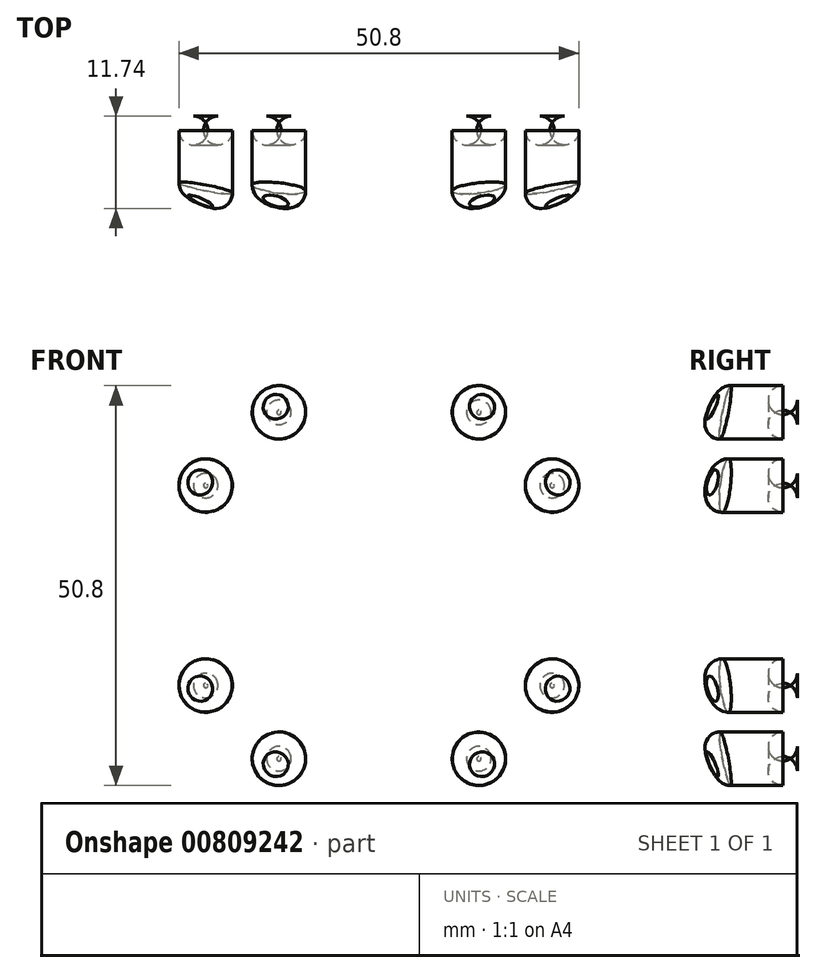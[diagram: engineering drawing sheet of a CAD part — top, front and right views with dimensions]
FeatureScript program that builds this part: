
annotation { "Feature Type Name" : "Feature", "Feature Type Description" : "" }
export const myFeature = defineFeature(function(context is Context, id is Id, definition is map)
    precondition{}
    {
        {
            var Q0;
            Q0=qCreatedBy(makeId("Front.planeOp"),FACE);
            var sketch = newSketch(context, id + "F0", { "sketchPlane" : qUnion([Q0])});
            skCircle(sketch, "E0", {"center": v(0, 0) * mm, "radius": 3.97 * mm});
            skCircle(sketch, "E1.cCircle", {"center": v(0, 0) * mm, "radius": 6.35 * mm, "construction": true});
            skLineSegment(sketch, "E1.0", {"start": v(-3.67, 6.35) * mm, "end": v(3.67, 6.35) * mm});
            skLineSegment(sketch, "E1.1", {"start": v(3.67, 6.35) * mm, "end": v(7.33, 0) * mm});
            skLineSegment(sketch, "E1.2", {"start": v(7.33, 0) * mm, "end": v(3.67, -6.35) * mm});
            skLineSegment(sketch, "E1.3", {"start": v(3.67, -6.35) * mm, "end": v(-3.67, -6.35) * mm});
            skLineSegment(sketch, "E1.4", {"start": v(-3.67, -6.35) * mm, "end": v(-7.33, 0) * mm});
            skLineSegment(sketch, "E1.5", {"start": v(-7.33, 0) * mm, "end": v(-3.67, 6.35) * mm});
            skPoint(sketch, "E1.0.midPoint", {"position": v(0, 6.35) * mm});
            skSolve(sketch);
        }
        {
            var Q0;
            Q0 = qSketchRegion(id + "F0", true);
            extrude(context, id + "F1", {"entities" : qUnion([Q0]), "depth" : 6.35 * mm, "offsetDistance" : 25.4 * mm});
        }
        {
            var Q0;
            Q0=qCreatedBy(makeId("Front.planeOp"),FACE);
            var sketch = newSketch(context, id + "F2", { "sketchPlane" : qUnion([Q0])});
            skLineSegment(sketch, "E2.0.0", {"start": v(-3.67, 6.35) * mm, "end": v(-7.33, 0) * mm});
            skLineSegment(sketch, "E2.0.1", {"start": v(-7.33, 0) * mm, "end": v(-3.67, -6.35) * mm});
            skLineSegment(sketch, "E2.0.2", {"start": v(-3.67, -6.35) * mm, "end": v(3.67, -6.35) * mm});
            skLineSegment(sketch, "E2.0.3", {"start": v(3.67, -6.35) * mm, "end": v(7.33, 0) * mm});
            skLineSegment(sketch, "E2.0.4", {"start": v(7.33, 0) * mm, "end": v(3.67, 6.35) * mm});
            skLineSegment(sketch, "E2.0.5", {"start": v(3.67, 6.35) * mm, "end": v(-3.67, 6.35) * mm});
            skCircle(sketch, "E3.cCircle", {"center": v(0, 0) * mm, "radius": 12.7 * mm, "construction": true});
            skLineSegment(sketch, "E3.1", {"start": v(3.4, 12.7) * mm, "end": v(9.3, 9.3) * mm});
            skLineSegment(sketch, "E3.2", {"start": v(9.3, 9.3) * mm, "end": v(12.7, 3.4) * mm});
            skLineSegment(sketch, "E3.3", {"start": v(12.7, 3.4) * mm, "end": v(12.7, -3.4) * mm});
            skLineSegment(sketch, "E3.4", {"start": v(12.7, -3.4) * mm, "end": v(9.3, -9.3) * mm});
            skLineSegment(sketch, "E3.5", {"start": v(9.3, -9.3) * mm, "end": v(3.4, -12.7) * mm});
            skLineSegment(sketch, "E3.6", {"start": v(3.4, -12.7) * mm, "end": v(-3.4, -12.7) * mm});
            skLineSegment(sketch, "E3.7", {"start": v(-3.4, -12.7) * mm, "end": v(-9.3, -9.3) * mm});
            skLineSegment(sketch, "E3.8", {"start": v(-9.3, -9.3) * mm, "end": v(-12.7, -3.4) * mm});
            skLineSegment(sketch, "E3.9", {"start": v(-12.7, -3.4) * mm, "end": v(-12.7, 3.4) * mm});
            skLineSegment(sketch, "E3.10", {"start": v(-12.7, 3.4) * mm, "end": v(-9.3, 9.3) * mm});
            skLineSegment(sketch, "E3.11", {"start": v(-9.3, 9.3) * mm, "end": v(-3.4, 12.7) * mm});
            skPoint(sketch, "E3.0.midPoint", {"position": v(0, 12.7) * mm});
            skLineSegment(sketch, "E4", {"start": v(-3.4, 12.7) * mm, "end": v(-3.4, 25.4) * mm});
            skLineSegment(sketch, "E5.bottom", {"start": v(3.4, 12.7) * mm, "end": v(-3.4, 12.7) * mm});
            skLineSegment(sketch, "E5.left", {"start": v(3.4, 12.7) * mm, "end": v(3.4, 25.4) * mm});
            skCircle(sketch, "E6", {"center": v(0, 25.4) * mm, "radius": 3.4 * mm});
            skCircle(sketch, "E7.1.0", {"center": v(-12.7, 22) * mm, "radius": 3.4 * mm});
            skLineSegment(sketch, "E7.1.1", {"start": v(-9.3, 9.3) * mm, "end": v(-15.65, 20.3) * mm});
            skLineSegment(sketch, "E7.1.2", {"start": v(-3.4, 12.7) * mm, "end": v(-9.75, 23.7) * mm});
            skCircle(sketch, "E7.2.0", {"center": v(-22, 12.7) * mm, "radius": 3.4 * mm});
            skLineSegment(sketch, "E7.2.1", {"start": v(-12.7, 3.4) * mm, "end": v(-23.7, 9.75) * mm});
            skLineSegment(sketch, "E7.2.2", {"start": v(-9.3, 9.3) * mm, "end": v(-20.3, 15.65) * mm});
            skCircle(sketch, "E7.3.0", {"center": v(-25.4, 0) * mm, "radius": 3.4 * mm});
            skLineSegment(sketch, "E7.3.1", {"start": v(-12.7, -3.4) * mm, "end": v(-25.4, -3.4) * mm});
            skLineSegment(sketch, "E7.3.2", {"start": v(-12.7, 3.4) * mm, "end": v(-25.4, 3.4) * mm});
            skCircle(sketch, "E7.4.0", {"center": v(-22, -12.7) * mm, "radius": 3.4 * mm});
            skLineSegment(sketch, "E7.4.1", {"start": v(-9.3, -9.3) * mm, "end": v(-20.3, -15.65) * mm});
            skLineSegment(sketch, "E7.4.2", {"start": v(-12.7, -3.4) * mm, "end": v(-23.7, -9.75) * mm});
            skCircle(sketch, "E7.5.0", {"center": v(-12.7, -22) * mm, "radius": 3.4 * mm});
            skLineSegment(sketch, "E7.5.1", {"start": v(-3.4, -12.7) * mm, "end": v(-9.75, -23.7) * mm});
            skLineSegment(sketch, "E7.5.2", {"start": v(-9.3, -9.3) * mm, "end": v(-15.65, -20.3) * mm});
            skCircle(sketch, "E7.6.0", {"center": v(0, -25.4) * mm, "radius": 3.4 * mm});
            skLineSegment(sketch, "E7.6.1", {"start": v(3.4, -12.7) * mm, "end": v(3.4, -25.4) * mm});
            skLineSegment(sketch, "E7.6.2", {"start": v(-3.4, -12.7) * mm, "end": v(-3.4, -25.4) * mm});
            skCircle(sketch, "E7.7.0", {"center": v(12.7, -22) * mm, "radius": 3.4 * mm});
            skLineSegment(sketch, "E7.7.1", {"start": v(9.3, -9.3) * mm, "end": v(15.65, -20.3) * mm});
            skLineSegment(sketch, "E7.7.2", {"start": v(3.4, -12.7) * mm, "end": v(9.75, -23.7) * mm});
            skCircle(sketch, "E7.8.0", {"center": v(22, -12.7) * mm, "radius": 3.4 * mm});
            skLineSegment(sketch, "E7.8.1", {"start": v(12.7, -3.4) * mm, "end": v(23.7, -9.75) * mm});
            skLineSegment(sketch, "E7.8.2", {"start": v(9.3, -9.3) * mm, "end": v(20.3, -15.65) * mm});
            skCircle(sketch, "E7.9.0", {"center": v(25.4, 0) * mm, "radius": 3.4 * mm});
            skLineSegment(sketch, "E7.9.1", {"start": v(12.7, 3.4) * mm, "end": v(25.4, 3.4) * mm});
            skLineSegment(sketch, "E7.9.2", {"start": v(12.7, -3.4) * mm, "end": v(25.4, -3.4) * mm});
            skCircle(sketch, "E7.10.0", {"center": v(22, 12.7) * mm, "radius": 3.4 * mm});
            skLineSegment(sketch, "E7.10.1", {"start": v(9.3, 9.3) * mm, "end": v(20.3, 15.65) * mm});
            skLineSegment(sketch, "E7.10.2", {"start": v(12.7, 3.4) * mm, "end": v(23.7, 9.75) * mm});
            skCircle(sketch, "E7.11.0", {"center": v(12.7, 22) * mm, "radius": 3.4 * mm});
            skLineSegment(sketch, "E7.11.1", {"start": v(3.4, 12.7) * mm, "end": v(9.75, 23.7) * mm});
            skLineSegment(sketch, "E7.11.2", {"start": v(9.3, 9.3) * mm, "end": v(15.65, 20.3) * mm});
            skSolve(sketch);
        }
        {
            var Q0;
            Q0 = qSketchRegion(id + "F2", true);
            extrude(context, id + "F3", {"entities" : qUnion([Q0]), "depth" : 6.35 * mm, "offsetDistance" : 25.4 * mm, "hasSecondDirection" : true, "secondDirectionOppositeDirection" : true, "secondDirectionDepth" : 6.35 * mm});
        }
        {
            var Q0;
            Q0=makeQuery(id+"F1.opExtrude","CAP_FACE",FACE,{"disambiguationData":[OSD([sQuery(id+"F0.wireOp",EDGE,"E0"),sQuery(id+"F0.wireOp",EDGE,"E1.0"),sQuery(id+"F0.wireOp",EDGE,"E1.1"),sQuery(id+"F0.wireOp",EDGE,"E1.2"),sQuery(id+"F0.wireOp",EDGE,"E1.3"),sQuery(id+"F0.wireOp",EDGE,"E1.4"),sQuery(id+"F0.wireOp",EDGE,"E1.5")])],"isStart":true});
            extrude(context, id + "F4", {"entities" : qUnion([Q0]), "operationType" : NewBodyOperationType.ADD, "depth" : 6.35 * mm, "offsetDistance" : 25.4 * mm});
        }
        {
            var Q0;
            {var subQ0=sQuery(id+"F2.wireOp",EDGE,"E7.1.0");var subQ1=makeQuery(id+"F2.imprint","INTERSECT",VERTEX,{"derivedFrom":[subQ0,sQuery(id+"F2.wireOp",EDGE,"E7.1.1")]});Q0=makeQuery(id+"F2.imprint","IMPRINT",FACE,{"disambiguationData":[TD([[makeQuery(id+"F2.imprint","IMPRINT",EDGE,{"disambiguationData":[TD([[subQ1,1.0]])],"derivedFrom":subQ0}),1.0]])]});}
            var Q1;
            {var subQ0=sQuery(id+"F2.wireOp",EDGE,"E6");var subQ1=makeQuery(id+"F2.imprint","INTERSECT",VERTEX,{"derivedFrom":[sQuery(id+"F2.wireOp",EDGE,"E5.left"),subQ0]});Q1=makeQuery(id+"F2.imprint","IMPRINT",FACE,{"disambiguationData":[TD([[makeQuery(id+"F2.imprint","IMPRINT",EDGE,{"disambiguationData":[TD([[subQ1,-1.0]])],"derivedFrom":subQ0}),1.0]])]});}
            var Q2;
            {var subQ0=sQuery(id+"F2.wireOp",EDGE,"E7.11.0");var subQ1=makeQuery(id+"F2.imprint","INTERSECT",VERTEX,{"derivedFrom":[subQ0,sQuery(id+"F2.wireOp",EDGE,"E7.11.1")]});Q2=makeQuery(id+"F2.imprint","IMPRINT",FACE,{"disambiguationData":[TD([[makeQuery(id+"F2.imprint","IMPRINT",EDGE,{"disambiguationData":[TD([[subQ1,1.0]])],"derivedFrom":subQ0}),1.0]])]});}
            var Q3;
            {var subQ0=sQuery(id+"F2.wireOp",EDGE,"E7.2.0");var subQ1=makeQuery(id+"F2.imprint","INTERSECT",VERTEX,{"derivedFrom":[subQ0,sQuery(id+"F2.wireOp",EDGE,"E7.2.1")]});Q3=makeQuery(id+"F2.imprint","IMPRINT",FACE,{"disambiguationData":[TD([[makeQuery(id+"F2.imprint","IMPRINT",EDGE,{"disambiguationData":[TD([[subQ1,1.0]])],"derivedFrom":subQ0}),1.0]])]});}
            var Q4;
            {var subQ0=sQuery(id+"F2.wireOp",EDGE,"E7.3.0");var subQ1=makeQuery(id+"F2.imprint","INTERSECT",VERTEX,{"derivedFrom":[subQ0,sQuery(id+"F2.wireOp",EDGE,"E7.3.1")]});Q4=makeQuery(id+"F2.imprint","IMPRINT",FACE,{"disambiguationData":[TD([[makeQuery(id+"F2.imprint","IMPRINT",EDGE,{"disambiguationData":[TD([[subQ1,1.0]])],"derivedFrom":subQ0}),1.0]])]});}
            var Q5;
            {var subQ0=sQuery(id+"F2.wireOp",EDGE,"E7.4.0");var subQ1=makeQuery(id+"F2.imprint","INTERSECT",VERTEX,{"derivedFrom":[subQ0,sQuery(id+"F2.wireOp",EDGE,"E7.4.1")]});Q5=makeQuery(id+"F2.imprint","IMPRINT",FACE,{"disambiguationData":[TD([[makeQuery(id+"F2.imprint","IMPRINT",EDGE,{"disambiguationData":[TD([[subQ1,1.0]])],"derivedFrom":subQ0}),1.0]])]});}
            var Q6;
            {var subQ0=sQuery(id+"F2.wireOp",EDGE,"E7.5.0");var subQ1=makeQuery(id+"F2.imprint","INTERSECT",VERTEX,{"derivedFrom":[subQ0,sQuery(id+"F2.wireOp",EDGE,"E7.5.1")]});Q6=makeQuery(id+"F2.imprint","IMPRINT",FACE,{"disambiguationData":[TD([[makeQuery(id+"F2.imprint","IMPRINT",EDGE,{"disambiguationData":[TD([[subQ1,1.0]])],"derivedFrom":subQ0}),1.0]])]});}
            var Q7;
            {var subQ0=sQuery(id+"F2.wireOp",EDGE,"E7.6.0");var subQ1=makeQuery(id+"F2.imprint","INTERSECT",VERTEX,{"derivedFrom":[subQ0,sQuery(id+"F2.wireOp",EDGE,"E7.6.1")]});Q7=makeQuery(id+"F2.imprint","IMPRINT",FACE,{"disambiguationData":[TD([[makeQuery(id+"F2.imprint","IMPRINT",EDGE,{"disambiguationData":[TD([[subQ1,1.0]])],"derivedFrom":subQ0}),1.0]])]});}
            var Q8;
            {var subQ0=sQuery(id+"F2.wireOp",EDGE,"E7.7.0");var subQ1=makeQuery(id+"F2.imprint","INTERSECT",VERTEX,{"derivedFrom":[subQ0,sQuery(id+"F2.wireOp",EDGE,"E7.7.1")]});Q8=makeQuery(id+"F2.imprint","IMPRINT",FACE,{"disambiguationData":[TD([[makeQuery(id+"F2.imprint","IMPRINT",EDGE,{"disambiguationData":[TD([[subQ1,1.0]])],"derivedFrom":subQ0}),1.0]])]});}
            var Q9;
            {var subQ0=sQuery(id+"F2.wireOp",EDGE,"E7.8.0");var subQ1=makeQuery(id+"F2.imprint","INTERSECT",VERTEX,{"derivedFrom":[subQ0,sQuery(id+"F2.wireOp",EDGE,"E7.8.1")]});Q9=makeQuery(id+"F2.imprint","IMPRINT",FACE,{"disambiguationData":[TD([[makeQuery(id+"F2.imprint","IMPRINT",EDGE,{"disambiguationData":[TD([[subQ1,1.0]])],"derivedFrom":subQ0}),1.0]])]});}
            var Q10;
            {var subQ0=sQuery(id+"F2.wireOp",EDGE,"E7.9.0");var subQ1=makeQuery(id+"F2.imprint","INTERSECT",VERTEX,{"derivedFrom":[subQ0,sQuery(id+"F2.wireOp",EDGE,"E7.9.1")]});Q10=makeQuery(id+"F2.imprint","IMPRINT",FACE,{"disambiguationData":[TD([[makeQuery(id+"F2.imprint","IMPRINT",EDGE,{"disambiguationData":[TD([[subQ1,1.0]])],"derivedFrom":subQ0}),1.0]])]});}
            var Q11;
            {var subQ0=sQuery(id+"F2.wireOp",EDGE,"E7.10.0");var subQ1=makeQuery(id+"F2.imprint","INTERSECT",VERTEX,{"derivedFrom":[subQ0,sQuery(id+"F2.wireOp",EDGE,"E7.10.1")]});Q11=makeQuery(id+"F2.imprint","IMPRINT",FACE,{"disambiguationData":[TD([[makeQuery(id+"F2.imprint","IMPRINT",EDGE,{"disambiguationData":[TD([[subQ1,1.0]])],"derivedFrom":subQ0}),1.0]])]});}
            extrude(context, id + "F5", {"entities" : qUnion([Q0, Q1, Q2, Q3, Q4, Q5, Q6, Q7, Q8, Q9, Q10, Q11]), "operationType" : NewBodyOperationType.ADD, "oppositeDirection" : true, "depth" : 12.7 * mm, "offsetDistance" : 25.4 * mm});
        }
        {
            var Q0;
            Q0=qCreatedBy(makeId("Right.planeOp"),FACE);
            var sketch = newSketch(context, id + "F6", { "sketchPlane" : qUnion([Q0])});
            skPoint(sketch, "E8.0", {"position": v(-6.35, 6.35) * mm});
            skPoint(sketch, "E9.0", {"position": v(-6.35, 9.3) * mm});
            skLineSegment(sketch, "E10", {"start": v(-6.35, 28.8) * mm, "end": v(12.7, 28.8) * mm});
            skPoint(sketch, "E11.0", {"position": v(6.35, 20.3) * mm});
            skLineSegment(sketch, "E12", {"start": v(6.35, 20.3) * mm, "end": v(6.35, 28.8) * mm, "construction": true});
            skLineSegment(sketch, "E13", {"start": v(3.17, 28.8) * mm, "end": v(-6.35, 9.3) * mm});
            skLineSegment(sketch, "E14", {"start": v(3.17, 28.8) * mm, "end": v(3.17, 31.54) * mm});
            skLineSegment(sketch, "E15", {"start": v(3.17, 31.54) * mm, "end": v(-9.41, 31.54) * mm});
            skLineSegment(sketch, "E16", {"start": v(-9.41, 31.54) * mm, "end": v(-8.74, 8.57) * mm});
            skLineSegment(sketch, "E17", {"start": v(-8.74, 8.57) * mm, "end": v(-6.35, 9.3) * mm});
            skSolve(sketch);
        }
        {
            var Q0;
            Q0 = qSketchRegion(id + "F6", true);
            var Q1;
            Q1=makeQuery(id+"F1.opExtrude","SWEPT_FACE",FACE,{"disambiguationData":[OSD([sQuery(id+"F0.wireOp",EDGE,"E0")])]});
            revolve(context, id + "F7", {"operationType" : NewBodyOperationType.REMOVE, "surfaceOperationType" : NewSurfaceOperationType.NEW, "entities" : qUnion([Q0]), "axis" : qUnion([Q1]), "revolveType" : RevolveType.FULL, "oppositeDirection" : true});
        }
        {
            var Q0;
            Q0=makeQuery(id+"F3.opExtrude","CAP_EDGE",EDGE,{"disambiguationData":[OSD([sQuery(id+"F2.wireOp",EDGE,"E4")])],"isStart":true});
            var Q1;
            Q1=makeQuery(id+"F3.opExtrude","CAP_EDGE",EDGE,{"disambiguationData":[OSD([sQuery(id+"F2.wireOp",EDGE,"E7.1.2")])],"isStart":true});
            var Q2;
            Q2=makeQuery(id+"F3.opExtrude","CAP_EDGE",EDGE,{"disambiguationData":[OSD([sQuery(id+"F2.wireOp",EDGE,"E7.2.2")])],"isStart":true});
            var Q3;
            Q3=makeQuery(id+"F3.opExtrude","CAP_EDGE",EDGE,{"disambiguationData":[OSD([sQuery(id+"F2.wireOp",EDGE,"E7.1.1")])],"isStart":true});
            var Q4;
            Q4=makeQuery(id+"F3.opExtrude","CAP_EDGE",EDGE,{"disambiguationData":[OSD([sQuery(id+"F2.wireOp",EDGE,"E7.2.1")])],"isStart":true});
            var Q5;
            Q5=makeQuery(id+"F3.opExtrude","CAP_EDGE",EDGE,{"disambiguationData":[OSD([sQuery(id+"F2.wireOp",EDGE,"E7.3.2")])],"isStart":true});
            var Q6;
            Q6=makeQuery(id+"F3.opExtrude","CAP_EDGE",EDGE,{"disambiguationData":[OSD([sQuery(id+"F2.wireOp",EDGE,"E7.3.1")])],"isStart":true});
            var Q7;
            Q7=makeQuery(id+"F3.opExtrude","CAP_EDGE",EDGE,{"disambiguationData":[OSD([sQuery(id+"F2.wireOp",EDGE,"E7.4.2")])],"isStart":true});
            var Q8;
            Q8=makeQuery(id+"F3.opExtrude","CAP_EDGE",EDGE,{"disambiguationData":[OSD([sQuery(id+"F2.wireOp",EDGE,"E7.4.1")])],"isStart":true});
            var Q9;
            Q9=makeQuery(id+"F3.opExtrude","CAP_EDGE",EDGE,{"disambiguationData":[OSD([sQuery(id+"F2.wireOp",EDGE,"E7.5.2")])],"isStart":true});
            var Q10;
            Q10=makeQuery(id+"F3.opExtrude","CAP_EDGE",EDGE,{"disambiguationData":[OSD([sQuery(id+"F2.wireOp",EDGE,"E7.6.2")])],"isStart":true});
            var Q11;
            Q11=makeQuery(id+"F3.opExtrude","CAP_EDGE",EDGE,{"disambiguationData":[OSD([sQuery(id+"F2.wireOp",EDGE,"E7.5.1")])],"isStart":true});
            var Q12;
            Q12=makeQuery(id+"F3.opExtrude","CAP_EDGE",EDGE,{"disambiguationData":[OSD([sQuery(id+"F2.wireOp",EDGE,"E7.6.1")])],"isStart":true});
            var Q13;
            Q13=makeQuery(id+"F3.opExtrude","CAP_EDGE",EDGE,{"disambiguationData":[OSD([sQuery(id+"F2.wireOp",EDGE,"E7.7.2")])],"isStart":true});
            var Q14;
            Q14=makeQuery(id+"F3.opExtrude","CAP_EDGE",EDGE,{"disambiguationData":[OSD([sQuery(id+"F2.wireOp",EDGE,"E7.8.2")])],"isStart":true});
            var Q15;
            Q15=makeQuery(id+"F3.opExtrude","CAP_EDGE",EDGE,{"disambiguationData":[OSD([sQuery(id+"F2.wireOp",EDGE,"E7.7.1")])],"isStart":true});
            var Q16;
            Q16=makeQuery(id+"F3.opExtrude","CAP_EDGE",EDGE,{"disambiguationData":[OSD([sQuery(id+"F2.wireOp",EDGE,"E7.9.2")])],"isStart":true});
            var Q17;
            Q17=makeQuery(id+"F3.opExtrude","CAP_EDGE",EDGE,{"disambiguationData":[OSD([sQuery(id+"F2.wireOp",EDGE,"E7.8.1")])],"isStart":true});
            var Q18;
            Q18=makeQuery(id+"F3.opExtrude","CAP_EDGE",EDGE,{"disambiguationData":[OSD([sQuery(id+"F2.wireOp",EDGE,"E7.10.2")])],"isStart":true});
            var Q19;
            Q19=makeQuery(id+"F3.opExtrude","CAP_EDGE",EDGE,{"disambiguationData":[OSD([sQuery(id+"F2.wireOp",EDGE,"E7.9.1")])],"isStart":true});
            var Q20;
            Q20=makeQuery(id+"F3.opExtrude","CAP_EDGE",EDGE,{"disambiguationData":[OSD([sQuery(id+"F2.wireOp",EDGE,"E7.10.1")])],"isStart":true});
            var Q21;
            Q21=makeQuery(id+"F3.opExtrude","CAP_EDGE",EDGE,{"disambiguationData":[OSD([sQuery(id+"F2.wireOp",EDGE,"E7.11.2")])],"isStart":true});
            var Q22;
            Q22=makeQuery(id+"F3.opExtrude","CAP_EDGE",EDGE,{"disambiguationData":[OSD([sQuery(id+"F2.wireOp",EDGE,"E7.11.1")])],"isStart":true});
            var Q23;
            Q23=makeQuery(id+"F3.opExtrude","CAP_EDGE",EDGE,{"disambiguationData":[OSD([sQuery(id+"F2.wireOp",EDGE,"E5.left")])],"isStart":true});
            var Q24;
            Q24=makeQuery(id+"F5.opExtrude","CAP_EDGE",EDGE,{"disambiguationData":[OSD([sQuery(id+"F2.wireOp",EDGE,"E7.11.0")])],"isStart":false});
            var Q25;
            Q25=makeQuery(id+"F5.opExtrude","CAP_FACE",FACE,{"disambiguationData":[OSD([sQuery(id+"F2.wireOp",EDGE,"E7.10.0")])],"isStart":false});
            var Q26;
            Q26=makeQuery(id+"F5.opExtrude","CAP_FACE",FACE,{"disambiguationData":[OSD([sQuery(id+"F2.wireOp",EDGE,"E7.9.0")])],"isStart":false});
            var Q27;
            Q27=makeQuery(id+"F5.opExtrude","CAP_FACE",FACE,{"disambiguationData":[OSD([sQuery(id+"F2.wireOp",EDGE,"E7.8.0")])],"isStart":false});
            var Q28;
            Q28=makeQuery(id+"F5.opExtrude","CAP_FACE",FACE,{"disambiguationData":[OSD([sQuery(id+"F2.wireOp",EDGE,"E7.7.0")])],"isStart":false});
            var Q29;
            Q29=makeQuery(id+"F5.opExtrude","CAP_FACE",FACE,{"disambiguationData":[OSD([sQuery(id+"F2.wireOp",EDGE,"E7.6.0")])],"isStart":false});
            var Q30;
            Q30=makeQuery(id+"F5.opExtrude","CAP_FACE",FACE,{"disambiguationData":[OSD([sQuery(id+"F2.wireOp",EDGE,"E7.5.0")])],"isStart":false});
            var Q31;
            Q31=makeQuery(id+"F5.opExtrude","CAP_EDGE",EDGE,{"disambiguationData":[OSD([sQuery(id+"F2.wireOp",EDGE,"E7.4.0")])],"isStart":false});
            var Q32;
            Q32=makeQuery(id+"F5.opExtrude","CAP_FACE",FACE,{"disambiguationData":[OSD([sQuery(id+"F2.wireOp",EDGE,"E7.3.0")])],"isStart":false});
            var Q33;
            Q33=makeQuery(id+"F5.opExtrude","CAP_FACE",FACE,{"disambiguationData":[OSD([sQuery(id+"F2.wireOp",EDGE,"E7.2.0")])],"isStart":false});
            var Q34;
            Q34=makeQuery(id+"F5.opExtrude","CAP_FACE",FACE,{"disambiguationData":[OSD([sQuery(id+"F2.wireOp",EDGE,"E7.1.0")])],"isStart":false});
            var Q35;
            Q35=makeQuery(id+"F5.opExtrude","CAP_FACE",FACE,{"disambiguationData":[OSD([sQuery(id+"F2.wireOp",EDGE,"E6")])],"isStart":false});
            var Q36;
            Q36=makeQuery(id+"F7.boolean.opBoolean","COPY",FACE,{"derivedFrom":makeQuery(id+"F7.opRevolve","SWEPT_FACE",FACE,{"disambiguationData":[OSD([sQuery(id+"F6.wireOp",EDGE,"E13")])]})});
            fillet(context, id + "F8", {"entities" : qUnion([Q0, Q1, Q2, Q3, Q4, Q5, Q6, Q7, Q8, Q9, Q10, Q11, Q12, Q13, Q14, Q15, Q16, Q17, Q18, Q19, Q20, Q21, Q22, Q23, Q24, Q25, Q26, Q27, Q28, Q29, Q30, Q31, Q32, Q33, Q34, Q35, Q36]), "radius" : 1.84 * mm, "tangentPropagation" : true, "allowEdgeOverflow" : false});
        }
        {
            var Q0;
            Q0=makeQuery(id+"F4.opExtrude","CAP_EDGE",EDGE,{"disambiguationData":[OSD([sQuery(id+"F0.wireOp",EDGE,"E0")])],"isStart":false});
            var Q1;
            Q1=makeQuery(id+"F3.opExtrude","CAP_FACE",FACE,{"disambiguationData":[OSD([sQuery(id+"F2.wireOp",EDGE,"E2.0.0"),sQuery(id+"F2.wireOp",EDGE,"E2.0.1"),sQuery(id+"F2.wireOp",EDGE,"E2.0.2"),sQuery(id+"F2.wireOp",EDGE,"E2.0.3"),sQuery(id+"F2.wireOp",EDGE,"E2.0.4"),sQuery(id+"F2.wireOp",EDGE,"E2.0.5"),sQuery(id+"F2.wireOp",EDGE,"E5.left"),sQuery(id+"F2.wireOp",EDGE,"E4"),sQuery(id+"F2.wireOp",EDGE,"E6"),sQuery(id+"F2.wireOp",EDGE,"E7.1.0"),sQuery(id+"F2.wireOp",EDGE,"E7.1.1"),sQuery(id+"F2.wireOp",EDGE,"E7.1.2"),sQuery(id+"F2.wireOp",EDGE,"E7.2.0"),sQuery(id+"F2.wireOp",EDGE,"E7.2.1"),sQuery(id+"F2.wireOp",EDGE,"E7.2.2"),sQuery(id+"F2.wireOp",EDGE,"E7.3.0"),sQuery(id+"F2.wireOp",EDGE,"E7.3.1"),sQuery(id+"F2.wireOp",EDGE,"E7.3.2"),sQuery(id+"F2.wireOp",EDGE,"E7.4.0"),sQuery(id+"F2.wireOp",EDGE,"E7.4.1"),sQuery(id+"F2.wireOp",EDGE,"E7.4.2"),sQuery(id+"F2.wireOp",EDGE,"E7.5.0"),sQuery(id+"F2.wireOp",EDGE,"E7.5.1"),sQuery(id+"F2.wireOp",EDGE,"E7.5.2"),sQuery(id+"F2.wireOp",EDGE,"E7.6.0"),sQuery(id+"F2.wireOp",EDGE,"E7.6.1"),sQuery(id+"F2.wireOp",EDGE,"E7.6.2"),sQuery(id+"F2.wireOp",EDGE,"E7.7.0"),sQuery(id+"F2.wireOp",EDGE,"E7.7.1"),sQuery(id+"F2.wireOp",EDGE,"E7.7.2"),sQuery(id+"F2.wireOp",EDGE,"E7.8.0"),sQuery(id+"F2.wireOp",EDGE,"E7.8.1"),sQuery(id+"F2.wireOp",EDGE,"E7.8.2"),sQuery(id+"F2.wireOp",EDGE,"E7.9.0"),sQuery(id+"F2.wireOp",EDGE,"E7.9.1"),sQuery(id+"F2.wireOp",EDGE,"E7.9.2"),sQuery(id+"F2.wireOp",EDGE,"E7.10.0"),sQuery(id+"F2.wireOp",EDGE,"E7.10.1"),sQuery(id+"F2.wireOp",EDGE,"E7.10.2"),sQuery(id+"F2.wireOp",EDGE,"E7.11.0"),sQuery(id+"F2.wireOp",EDGE,"E7.11.1"),sQuery(id+"F2.wireOp",EDGE,"E7.11.2")])],"isStart":false});
            var Q2;
            Q2=makeQuery(id+"F4.opExtrude","CAP_EDGE",EDGE,{"disambiguationData":[OSD([sQuery(id+"F0.wireOp",EDGE,"E0")])],"isStart":true});
            chamfer(context, id + "F9", {"entities" : qUnion([Q0, Q1, Q2]), "width" : 0.5 * mm, "tangentPropagation" : true});
        }
        {
            var Q0;
            {var subQ0=sQuery(id+"F2.wireOp",EDGE,"E7.9.0");Q0=makeQuery(id+"F5.boolean.opBoolean","INTERSECT",EDGE,{"derivedFrom":[makeQuery(id+"F4.boolean.opBoolean","MERGE",FACE,{"derivedFrom":[makeQuery(id+"F3.opExtrude","CAP_FACE",FACE,{"disambiguationData":[OSD([sQuery(id+"F2.wireOp",EDGE,"E2.0.0"),sQuery(id+"F2.wireOp",EDGE,"E2.0.1"),sQuery(id+"F2.wireOp",EDGE,"E2.0.2"),sQuery(id+"F2.wireOp",EDGE,"E2.0.3"),sQuery(id+"F2.wireOp",EDGE,"E2.0.4"),sQuery(id+"F2.wireOp",EDGE,"E2.0.5"),sQuery(id+"F2.wireOp",EDGE,"E5.left"),sQuery(id+"F2.wireOp",EDGE,"E4"),sQuery(id+"F2.wireOp",EDGE,"E6"),sQuery(id+"F2.wireOp",EDGE,"E7.1.0"),sQuery(id+"F2.wireOp",EDGE,"E7.1.1"),sQuery(id+"F2.wireOp",EDGE,"E7.1.2"),sQuery(id+"F2.wireOp",EDGE,"E7.2.0"),sQuery(id+"F2.wireOp",EDGE,"E7.2.1"),sQuery(id+"F2.wireOp",EDGE,"E7.2.2"),sQuery(id+"F2.wireOp",EDGE,"E7.3.0"),sQuery(id+"F2.wireOp",EDGE,"E7.3.1"),sQuery(id+"F2.wireOp",EDGE,"E7.3.2"),sQuery(id+"F2.wireOp",EDGE,"E7.4.0"),sQuery(id+"F2.wireOp",EDGE,"E7.4.1"),sQuery(id+"F2.wireOp",EDGE,"E7.4.2"),sQuery(id+"F2.wireOp",EDGE,"E7.5.0"),sQuery(id+"F2.wireOp",EDGE,"E7.5.1"),sQuery(id+"F2.wireOp",EDGE,"E7.5.2"),sQuery(id+"F2.wireOp",EDGE,"E7.6.0"),sQuery(id+"F2.wireOp",EDGE,"E7.6.1"),sQuery(id+"F2.wireOp",EDGE,"E7.6.2"),sQuery(id+"F2.wireOp",EDGE,"E7.7.0"),sQuery(id+"F2.wireOp",EDGE,"E7.7.1"),sQuery(id+"F2.wireOp",EDGE,"E7.7.2"),sQuery(id+"F2.wireOp",EDGE,"E7.8.0"),sQuery(id+"F2.wireOp",EDGE,"E7.8.1"),sQuery(id+"F2.wireOp",EDGE,"E7.8.2"),subQ0,sQuery(id+"F2.wireOp",EDGE,"E7.9.1"),sQuery(id+"F2.wireOp",EDGE,"E7.9.2"),sQuery(id+"F2.wireOp",EDGE,"E7.10.0"),sQuery(id+"F2.wireOp",EDGE,"E7.10.1"),sQuery(id+"F2.wireOp",EDGE,"E7.10.2"),sQuery(id+"F2.wireOp",EDGE,"E7.11.0"),sQuery(id+"F2.wireOp",EDGE,"E7.11.1"),sQuery(id+"F2.wireOp",EDGE,"E7.11.2")])],"isStart":true}),makeQuery(id+"F4.opExtrude","CAP_FACE",FACE,{"disambiguationData":[OSD([sQuery(id+"F0.wireOp",EDGE,"E0"),sQuery(id+"F0.wireOp",EDGE,"E1.0"),sQuery(id+"F0.wireOp",EDGE,"E1.1"),sQuery(id+"F0.wireOp",EDGE,"E1.2"),sQuery(id+"F0.wireOp",EDGE,"E1.3"),sQuery(id+"F0.wireOp",EDGE,"E1.4"),sQuery(id+"F0.wireOp",EDGE,"E1.5")])],"isStart":false})]}),makeQuery(id+"F5.opExtrude","SWEPT_FACE",FACE,{"disambiguationData":[OSD([subQ0])]})]});}
            var Q1;
            {var subQ0=sQuery(id+"F2.wireOp",EDGE,"E7.11.0");Q1=makeQuery(id+"F5.boolean.opBoolean","INTERSECT",EDGE,{"derivedFrom":[makeQuery(id+"F4.boolean.opBoolean","MERGE",FACE,{"derivedFrom":[makeQuery(id+"F3.opExtrude","CAP_FACE",FACE,{"disambiguationData":[OSD([sQuery(id+"F2.wireOp",EDGE,"E2.0.0"),sQuery(id+"F2.wireOp",EDGE,"E2.0.1"),sQuery(id+"F2.wireOp",EDGE,"E2.0.2"),sQuery(id+"F2.wireOp",EDGE,"E2.0.3"),sQuery(id+"F2.wireOp",EDGE,"E2.0.4"),sQuery(id+"F2.wireOp",EDGE,"E2.0.5"),sQuery(id+"F2.wireOp",EDGE,"E5.left"),sQuery(id+"F2.wireOp",EDGE,"E4"),sQuery(id+"F2.wireOp",EDGE,"E6"),sQuery(id+"F2.wireOp",EDGE,"E7.1.0"),sQuery(id+"F2.wireOp",EDGE,"E7.1.1"),sQuery(id+"F2.wireOp",EDGE,"E7.1.2"),sQuery(id+"F2.wireOp",EDGE,"E7.2.0"),sQuery(id+"F2.wireOp",EDGE,"E7.2.1"),sQuery(id+"F2.wireOp",EDGE,"E7.2.2"),sQuery(id+"F2.wireOp",EDGE,"E7.3.0"),sQuery(id+"F2.wireOp",EDGE,"E7.3.1"),sQuery(id+"F2.wireOp",EDGE,"E7.3.2"),sQuery(id+"F2.wireOp",EDGE,"E7.4.0"),sQuery(id+"F2.wireOp",EDGE,"E7.4.1"),sQuery(id+"F2.wireOp",EDGE,"E7.4.2"),sQuery(id+"F2.wireOp",EDGE,"E7.5.0"),sQuery(id+"F2.wireOp",EDGE,"E7.5.1"),sQuery(id+"F2.wireOp",EDGE,"E7.5.2"),sQuery(id+"F2.wireOp",EDGE,"E7.6.0"),sQuery(id+"F2.wireOp",EDGE,"E7.6.1"),sQuery(id+"F2.wireOp",EDGE,"E7.6.2"),sQuery(id+"F2.wireOp",EDGE,"E7.7.0"),sQuery(id+"F2.wireOp",EDGE,"E7.7.1"),sQuery(id+"F2.wireOp",EDGE,"E7.7.2"),sQuery(id+"F2.wireOp",EDGE,"E7.8.0"),sQuery(id+"F2.wireOp",EDGE,"E7.8.1"),sQuery(id+"F2.wireOp",EDGE,"E7.8.2"),sQuery(id+"F2.wireOp",EDGE,"E7.9.0"),sQuery(id+"F2.wireOp",EDGE,"E7.9.1"),sQuery(id+"F2.wireOp",EDGE,"E7.9.2"),sQuery(id+"F2.wireOp",EDGE,"E7.10.0"),sQuery(id+"F2.wireOp",EDGE,"E7.10.1"),sQuery(id+"F2.wireOp",EDGE,"E7.10.2"),subQ0,sQuery(id+"F2.wireOp",EDGE,"E7.11.1"),sQuery(id+"F2.wireOp",EDGE,"E7.11.2")])],"isStart":true}),makeQuery(id+"F4.opExtrude","CAP_FACE",FACE,{"disambiguationData":[OSD([sQuery(id+"F0.wireOp",EDGE,"E0"),sQuery(id+"F0.wireOp",EDGE,"E1.0"),sQuery(id+"F0.wireOp",EDGE,"E1.1"),sQuery(id+"F0.wireOp",EDGE,"E1.2"),sQuery(id+"F0.wireOp",EDGE,"E1.3"),sQuery(id+"F0.wireOp",EDGE,"E1.4"),sQuery(id+"F0.wireOp",EDGE,"E1.5")])],"isStart":false})]}),makeQuery(id+"F5.opExtrude","SWEPT_FACE",FACE,{"disambiguationData":[OSD([subQ0])]})]});}
            var Q2;
            {var subQ0=sQuery(id+"F2.wireOp",EDGE,"E6");Q2=makeQuery(id+"F5.boolean.opBoolean","INTERSECT",EDGE,{"derivedFrom":[makeQuery(id+"F4.boolean.opBoolean","MERGE",FACE,{"derivedFrom":[makeQuery(id+"F3.opExtrude","CAP_FACE",FACE,{"disambiguationData":[OSD([sQuery(id+"F2.wireOp",EDGE,"E2.0.0"),sQuery(id+"F2.wireOp",EDGE,"E2.0.1"),sQuery(id+"F2.wireOp",EDGE,"E2.0.2"),sQuery(id+"F2.wireOp",EDGE,"E2.0.3"),sQuery(id+"F2.wireOp",EDGE,"E2.0.4"),sQuery(id+"F2.wireOp",EDGE,"E2.0.5"),sQuery(id+"F2.wireOp",EDGE,"E5.left"),sQuery(id+"F2.wireOp",EDGE,"E4"),subQ0,sQuery(id+"F2.wireOp",EDGE,"E7.1.0"),sQuery(id+"F2.wireOp",EDGE,"E7.1.1"),sQuery(id+"F2.wireOp",EDGE,"E7.1.2"),sQuery(id+"F2.wireOp",EDGE,"E7.2.0"),sQuery(id+"F2.wireOp",EDGE,"E7.2.1"),sQuery(id+"F2.wireOp",EDGE,"E7.2.2"),sQuery(id+"F2.wireOp",EDGE,"E7.3.0"),sQuery(id+"F2.wireOp",EDGE,"E7.3.1"),sQuery(id+"F2.wireOp",EDGE,"E7.3.2"),sQuery(id+"F2.wireOp",EDGE,"E7.4.0"),sQuery(id+"F2.wireOp",EDGE,"E7.4.1"),sQuery(id+"F2.wireOp",EDGE,"E7.4.2"),sQuery(id+"F2.wireOp",EDGE,"E7.5.0"),sQuery(id+"F2.wireOp",EDGE,"E7.5.1"),sQuery(id+"F2.wireOp",EDGE,"E7.5.2"),sQuery(id+"F2.wireOp",EDGE,"E7.6.0"),sQuery(id+"F2.wireOp",EDGE,"E7.6.1"),sQuery(id+"F2.wireOp",EDGE,"E7.6.2"),sQuery(id+"F2.wireOp",EDGE,"E7.7.0"),sQuery(id+"F2.wireOp",EDGE,"E7.7.1"),sQuery(id+"F2.wireOp",EDGE,"E7.7.2"),sQuery(id+"F2.wireOp",EDGE,"E7.8.0"),sQuery(id+"F2.wireOp",EDGE,"E7.8.1"),sQuery(id+"F2.wireOp",EDGE,"E7.8.2"),sQuery(id+"F2.wireOp",EDGE,"E7.9.0"),sQuery(id+"F2.wireOp",EDGE,"E7.9.1"),sQuery(id+"F2.wireOp",EDGE,"E7.9.2"),sQuery(id+"F2.wireOp",EDGE,"E7.10.0"),sQuery(id+"F2.wireOp",EDGE,"E7.10.1"),sQuery(id+"F2.wireOp",EDGE,"E7.10.2"),sQuery(id+"F2.wireOp",EDGE,"E7.11.0"),sQuery(id+"F2.wireOp",EDGE,"E7.11.1"),sQuery(id+"F2.wireOp",EDGE,"E7.11.2")])],"isStart":true}),makeQuery(id+"F4.opExtrude","CAP_FACE",FACE,{"disambiguationData":[OSD([sQuery(id+"F0.wireOp",EDGE,"E0"),sQuery(id+"F0.wireOp",EDGE,"E1.0"),sQuery(id+"F0.wireOp",EDGE,"E1.1"),sQuery(id+"F0.wireOp",EDGE,"E1.2"),sQuery(id+"F0.wireOp",EDGE,"E1.3"),sQuery(id+"F0.wireOp",EDGE,"E1.4"),sQuery(id+"F0.wireOp",EDGE,"E1.5")])],"isStart":false})]}),makeQuery(id+"F5.opExtrude","SWEPT_FACE",FACE,{"disambiguationData":[OSD([subQ0])]})]});}
            var Q3;
            {var subQ0=sQuery(id+"F2.wireOp",EDGE,"E7.1.0");Q3=makeQuery(id+"F5.boolean.opBoolean","INTERSECT",EDGE,{"derivedFrom":[makeQuery(id+"F4.boolean.opBoolean","MERGE",FACE,{"derivedFrom":[makeQuery(id+"F3.opExtrude","CAP_FACE",FACE,{"disambiguationData":[OSD([sQuery(id+"F2.wireOp",EDGE,"E2.0.0"),sQuery(id+"F2.wireOp",EDGE,"E2.0.1"),sQuery(id+"F2.wireOp",EDGE,"E2.0.2"),sQuery(id+"F2.wireOp",EDGE,"E2.0.3"),sQuery(id+"F2.wireOp",EDGE,"E2.0.4"),sQuery(id+"F2.wireOp",EDGE,"E2.0.5"),sQuery(id+"F2.wireOp",EDGE,"E5.left"),sQuery(id+"F2.wireOp",EDGE,"E4"),sQuery(id+"F2.wireOp",EDGE,"E6"),subQ0,sQuery(id+"F2.wireOp",EDGE,"E7.1.1"),sQuery(id+"F2.wireOp",EDGE,"E7.1.2"),sQuery(id+"F2.wireOp",EDGE,"E7.2.0"),sQuery(id+"F2.wireOp",EDGE,"E7.2.1"),sQuery(id+"F2.wireOp",EDGE,"E7.2.2"),sQuery(id+"F2.wireOp",EDGE,"E7.3.0"),sQuery(id+"F2.wireOp",EDGE,"E7.3.1"),sQuery(id+"F2.wireOp",EDGE,"E7.3.2"),sQuery(id+"F2.wireOp",EDGE,"E7.4.0"),sQuery(id+"F2.wireOp",EDGE,"E7.4.1"),sQuery(id+"F2.wireOp",EDGE,"E7.4.2"),sQuery(id+"F2.wireOp",EDGE,"E7.5.0"),sQuery(id+"F2.wireOp",EDGE,"E7.5.1"),sQuery(id+"F2.wireOp",EDGE,"E7.5.2"),sQuery(id+"F2.wireOp",EDGE,"E7.6.0"),sQuery(id+"F2.wireOp",EDGE,"E7.6.1"),sQuery(id+"F2.wireOp",EDGE,"E7.6.2"),sQuery(id+"F2.wireOp",EDGE,"E7.7.0"),sQuery(id+"F2.wireOp",EDGE,"E7.7.1"),sQuery(id+"F2.wireOp",EDGE,"E7.7.2"),sQuery(id+"F2.wireOp",EDGE,"E7.8.0"),sQuery(id+"F2.wireOp",EDGE,"E7.8.1"),sQuery(id+"F2.wireOp",EDGE,"E7.8.2"),sQuery(id+"F2.wireOp",EDGE,"E7.9.0"),sQuery(id+"F2.wireOp",EDGE,"E7.9.1"),sQuery(id+"F2.wireOp",EDGE,"E7.9.2"),sQuery(id+"F2.wireOp",EDGE,"E7.10.0"),sQuery(id+"F2.wireOp",EDGE,"E7.10.1"),sQuery(id+"F2.wireOp",EDGE,"E7.10.2"),sQuery(id+"F2.wireOp",EDGE,"E7.11.0"),sQuery(id+"F2.wireOp",EDGE,"E7.11.1"),sQuery(id+"F2.wireOp",EDGE,"E7.11.2")])],"isStart":true}),makeQuery(id+"F4.opExtrude","CAP_FACE",FACE,{"disambiguationData":[OSD([sQuery(id+"F0.wireOp",EDGE,"E0"),sQuery(id+"F0.wireOp",EDGE,"E1.0"),sQuery(id+"F0.wireOp",EDGE,"E1.1"),sQuery(id+"F0.wireOp",EDGE,"E1.2"),sQuery(id+"F0.wireOp",EDGE,"E1.3"),sQuery(id+"F0.wireOp",EDGE,"E1.4"),sQuery(id+"F0.wireOp",EDGE,"E1.5")])],"isStart":false})]}),makeQuery(id+"F5.opExtrude","SWEPT_FACE",FACE,{"disambiguationData":[OSD([subQ0])]})]});}
            var Q4;
            {var subQ0=sQuery(id+"F2.wireOp",EDGE,"E7.2.0");Q4=makeQuery(id+"F5.boolean.opBoolean","INTERSECT",EDGE,{"derivedFrom":[makeQuery(id+"F4.boolean.opBoolean","MERGE",FACE,{"derivedFrom":[makeQuery(id+"F3.opExtrude","CAP_FACE",FACE,{"disambiguationData":[OSD([sQuery(id+"F2.wireOp",EDGE,"E2.0.0"),sQuery(id+"F2.wireOp",EDGE,"E2.0.1"),sQuery(id+"F2.wireOp",EDGE,"E2.0.2"),sQuery(id+"F2.wireOp",EDGE,"E2.0.3"),sQuery(id+"F2.wireOp",EDGE,"E2.0.4"),sQuery(id+"F2.wireOp",EDGE,"E2.0.5"),sQuery(id+"F2.wireOp",EDGE,"E5.left"),sQuery(id+"F2.wireOp",EDGE,"E4"),sQuery(id+"F2.wireOp",EDGE,"E6"),sQuery(id+"F2.wireOp",EDGE,"E7.1.0"),sQuery(id+"F2.wireOp",EDGE,"E7.1.1"),sQuery(id+"F2.wireOp",EDGE,"E7.1.2"),subQ0,sQuery(id+"F2.wireOp",EDGE,"E7.2.1"),sQuery(id+"F2.wireOp",EDGE,"E7.2.2"),sQuery(id+"F2.wireOp",EDGE,"E7.3.0"),sQuery(id+"F2.wireOp",EDGE,"E7.3.1"),sQuery(id+"F2.wireOp",EDGE,"E7.3.2"),sQuery(id+"F2.wireOp",EDGE,"E7.4.0"),sQuery(id+"F2.wireOp",EDGE,"E7.4.1"),sQuery(id+"F2.wireOp",EDGE,"E7.4.2"),sQuery(id+"F2.wireOp",EDGE,"E7.5.0"),sQuery(id+"F2.wireOp",EDGE,"E7.5.1"),sQuery(id+"F2.wireOp",EDGE,"E7.5.2"),sQuery(id+"F2.wireOp",EDGE,"E7.6.0"),sQuery(id+"F2.wireOp",EDGE,"E7.6.1"),sQuery(id+"F2.wireOp",EDGE,"E7.6.2"),sQuery(id+"F2.wireOp",EDGE,"E7.7.0"),sQuery(id+"F2.wireOp",EDGE,"E7.7.1"),sQuery(id+"F2.wireOp",EDGE,"E7.7.2"),sQuery(id+"F2.wireOp",EDGE,"E7.8.0"),sQuery(id+"F2.wireOp",EDGE,"E7.8.1"),sQuery(id+"F2.wireOp",EDGE,"E7.8.2"),sQuery(id+"F2.wireOp",EDGE,"E7.9.0"),sQuery(id+"F2.wireOp",EDGE,"E7.9.1"),sQuery(id+"F2.wireOp",EDGE,"E7.9.2"),sQuery(id+"F2.wireOp",EDGE,"E7.10.0"),sQuery(id+"F2.wireOp",EDGE,"E7.10.1"),sQuery(id+"F2.wireOp",EDGE,"E7.10.2"),sQuery(id+"F2.wireOp",EDGE,"E7.11.0"),sQuery(id+"F2.wireOp",EDGE,"E7.11.1"),sQuery(id+"F2.wireOp",EDGE,"E7.11.2")])],"isStart":true}),makeQuery(id+"F4.opExtrude","CAP_FACE",FACE,{"disambiguationData":[OSD([sQuery(id+"F0.wireOp",EDGE,"E0"),sQuery(id+"F0.wireOp",EDGE,"E1.0"),sQuery(id+"F0.wireOp",EDGE,"E1.1"),sQuery(id+"F0.wireOp",EDGE,"E1.2"),sQuery(id+"F0.wireOp",EDGE,"E1.3"),sQuery(id+"F0.wireOp",EDGE,"E1.4"),sQuery(id+"F0.wireOp",EDGE,"E1.5")])],"isStart":false})]}),makeQuery(id+"F5.opExtrude","SWEPT_FACE",FACE,{"disambiguationData":[OSD([subQ0])]})]});}
            var Q5;
            {var subQ0=sQuery(id+"F2.wireOp",EDGE,"E7.10.0");Q5=makeQuery(id+"F5.boolean.opBoolean","INTERSECT",EDGE,{"derivedFrom":[makeQuery(id+"F4.boolean.opBoolean","MERGE",FACE,{"derivedFrom":[makeQuery(id+"F3.opExtrude","CAP_FACE",FACE,{"disambiguationData":[OSD([sQuery(id+"F2.wireOp",EDGE,"E2.0.0"),sQuery(id+"F2.wireOp",EDGE,"E2.0.1"),sQuery(id+"F2.wireOp",EDGE,"E2.0.2"),sQuery(id+"F2.wireOp",EDGE,"E2.0.3"),sQuery(id+"F2.wireOp",EDGE,"E2.0.4"),sQuery(id+"F2.wireOp",EDGE,"E2.0.5"),sQuery(id+"F2.wireOp",EDGE,"E5.left"),sQuery(id+"F2.wireOp",EDGE,"E4"),sQuery(id+"F2.wireOp",EDGE,"E6"),sQuery(id+"F2.wireOp",EDGE,"E7.1.0"),sQuery(id+"F2.wireOp",EDGE,"E7.1.1"),sQuery(id+"F2.wireOp",EDGE,"E7.1.2"),sQuery(id+"F2.wireOp",EDGE,"E7.2.0"),sQuery(id+"F2.wireOp",EDGE,"E7.2.1"),sQuery(id+"F2.wireOp",EDGE,"E7.2.2"),sQuery(id+"F2.wireOp",EDGE,"E7.3.0"),sQuery(id+"F2.wireOp",EDGE,"E7.3.1"),sQuery(id+"F2.wireOp",EDGE,"E7.3.2"),sQuery(id+"F2.wireOp",EDGE,"E7.4.0"),sQuery(id+"F2.wireOp",EDGE,"E7.4.1"),sQuery(id+"F2.wireOp",EDGE,"E7.4.2"),sQuery(id+"F2.wireOp",EDGE,"E7.5.0"),sQuery(id+"F2.wireOp",EDGE,"E7.5.1"),sQuery(id+"F2.wireOp",EDGE,"E7.5.2"),sQuery(id+"F2.wireOp",EDGE,"E7.6.0"),sQuery(id+"F2.wireOp",EDGE,"E7.6.1"),sQuery(id+"F2.wireOp",EDGE,"E7.6.2"),sQuery(id+"F2.wireOp",EDGE,"E7.7.0"),sQuery(id+"F2.wireOp",EDGE,"E7.7.1"),sQuery(id+"F2.wireOp",EDGE,"E7.7.2"),sQuery(id+"F2.wireOp",EDGE,"E7.8.0"),sQuery(id+"F2.wireOp",EDGE,"E7.8.1"),sQuery(id+"F2.wireOp",EDGE,"E7.8.2"),sQuery(id+"F2.wireOp",EDGE,"E7.9.0"),sQuery(id+"F2.wireOp",EDGE,"E7.9.1"),sQuery(id+"F2.wireOp",EDGE,"E7.9.2"),subQ0,sQuery(id+"F2.wireOp",EDGE,"E7.10.1"),sQuery(id+"F2.wireOp",EDGE,"E7.10.2"),sQuery(id+"F2.wireOp",EDGE,"E7.11.0"),sQuery(id+"F2.wireOp",EDGE,"E7.11.1"),sQuery(id+"F2.wireOp",EDGE,"E7.11.2")])],"isStart":true}),makeQuery(id+"F4.opExtrude","CAP_FACE",FACE,{"disambiguationData":[OSD([sQuery(id+"F0.wireOp",EDGE,"E0"),sQuery(id+"F0.wireOp",EDGE,"E1.0"),sQuery(id+"F0.wireOp",EDGE,"E1.1"),sQuery(id+"F0.wireOp",EDGE,"E1.2"),sQuery(id+"F0.wireOp",EDGE,"E1.3"),sQuery(id+"F0.wireOp",EDGE,"E1.4"),sQuery(id+"F0.wireOp",EDGE,"E1.5")])],"isStart":false})]}),makeQuery(id+"F5.opExtrude","SWEPT_FACE",FACE,{"disambiguationData":[OSD([subQ0])]})]});}
            var Q6;
            {var subQ0=sQuery(id+"F2.wireOp",EDGE,"E7.8.0");Q6=makeQuery(id+"F5.boolean.opBoolean","INTERSECT",EDGE,{"derivedFrom":[makeQuery(id+"F4.boolean.opBoolean","MERGE",FACE,{"derivedFrom":[makeQuery(id+"F3.opExtrude","CAP_FACE",FACE,{"disambiguationData":[OSD([sQuery(id+"F2.wireOp",EDGE,"E2.0.0"),sQuery(id+"F2.wireOp",EDGE,"E2.0.1"),sQuery(id+"F2.wireOp",EDGE,"E2.0.2"),sQuery(id+"F2.wireOp",EDGE,"E2.0.3"),sQuery(id+"F2.wireOp",EDGE,"E2.0.4"),sQuery(id+"F2.wireOp",EDGE,"E2.0.5"),sQuery(id+"F2.wireOp",EDGE,"E5.left"),sQuery(id+"F2.wireOp",EDGE,"E4"),sQuery(id+"F2.wireOp",EDGE,"E6"),sQuery(id+"F2.wireOp",EDGE,"E7.1.0"),sQuery(id+"F2.wireOp",EDGE,"E7.1.1"),sQuery(id+"F2.wireOp",EDGE,"E7.1.2"),sQuery(id+"F2.wireOp",EDGE,"E7.2.0"),sQuery(id+"F2.wireOp",EDGE,"E7.2.1"),sQuery(id+"F2.wireOp",EDGE,"E7.2.2"),sQuery(id+"F2.wireOp",EDGE,"E7.3.0"),sQuery(id+"F2.wireOp",EDGE,"E7.3.1"),sQuery(id+"F2.wireOp",EDGE,"E7.3.2"),sQuery(id+"F2.wireOp",EDGE,"E7.4.0"),sQuery(id+"F2.wireOp",EDGE,"E7.4.1"),sQuery(id+"F2.wireOp",EDGE,"E7.4.2"),sQuery(id+"F2.wireOp",EDGE,"E7.5.0"),sQuery(id+"F2.wireOp",EDGE,"E7.5.1"),sQuery(id+"F2.wireOp",EDGE,"E7.5.2"),sQuery(id+"F2.wireOp",EDGE,"E7.6.0"),sQuery(id+"F2.wireOp",EDGE,"E7.6.1"),sQuery(id+"F2.wireOp",EDGE,"E7.6.2"),sQuery(id+"F2.wireOp",EDGE,"E7.7.0"),sQuery(id+"F2.wireOp",EDGE,"E7.7.1"),sQuery(id+"F2.wireOp",EDGE,"E7.7.2"),subQ0,sQuery(id+"F2.wireOp",EDGE,"E7.8.1"),sQuery(id+"F2.wireOp",EDGE,"E7.8.2"),sQuery(id+"F2.wireOp",EDGE,"E7.9.0"),sQuery(id+"F2.wireOp",EDGE,"E7.9.1"),sQuery(id+"F2.wireOp",EDGE,"E7.9.2"),sQuery(id+"F2.wireOp",EDGE,"E7.10.0"),sQuery(id+"F2.wireOp",EDGE,"E7.10.1"),sQuery(id+"F2.wireOp",EDGE,"E7.10.2"),sQuery(id+"F2.wireOp",EDGE,"E7.11.0"),sQuery(id+"F2.wireOp",EDGE,"E7.11.1"),sQuery(id+"F2.wireOp",EDGE,"E7.11.2")])],"isStart":true}),makeQuery(id+"F4.opExtrude","CAP_FACE",FACE,{"disambiguationData":[OSD([sQuery(id+"F0.wireOp",EDGE,"E0"),sQuery(id+"F0.wireOp",EDGE,"E1.0"),sQuery(id+"F0.wireOp",EDGE,"E1.1"),sQuery(id+"F0.wireOp",EDGE,"E1.2"),sQuery(id+"F0.wireOp",EDGE,"E1.3"),sQuery(id+"F0.wireOp",EDGE,"E1.4"),sQuery(id+"F0.wireOp",EDGE,"E1.5")])],"isStart":false})]}),makeQuery(id+"F5.opExtrude","SWEPT_FACE",FACE,{"disambiguationData":[OSD([subQ0])]})]});}
            var Q7;
            {var subQ0=sQuery(id+"F2.wireOp",EDGE,"E7.7.0");Q7=makeQuery(id+"F5.boolean.opBoolean","INTERSECT",EDGE,{"derivedFrom":[makeQuery(id+"F4.boolean.opBoolean","MERGE",FACE,{"derivedFrom":[makeQuery(id+"F3.opExtrude","CAP_FACE",FACE,{"disambiguationData":[OSD([sQuery(id+"F2.wireOp",EDGE,"E2.0.0"),sQuery(id+"F2.wireOp",EDGE,"E2.0.1"),sQuery(id+"F2.wireOp",EDGE,"E2.0.2"),sQuery(id+"F2.wireOp",EDGE,"E2.0.3"),sQuery(id+"F2.wireOp",EDGE,"E2.0.4"),sQuery(id+"F2.wireOp",EDGE,"E2.0.5"),sQuery(id+"F2.wireOp",EDGE,"E5.left"),sQuery(id+"F2.wireOp",EDGE,"E4"),sQuery(id+"F2.wireOp",EDGE,"E6"),sQuery(id+"F2.wireOp",EDGE,"E7.1.0"),sQuery(id+"F2.wireOp",EDGE,"E7.1.1"),sQuery(id+"F2.wireOp",EDGE,"E7.1.2"),sQuery(id+"F2.wireOp",EDGE,"E7.2.0"),sQuery(id+"F2.wireOp",EDGE,"E7.2.1"),sQuery(id+"F2.wireOp",EDGE,"E7.2.2"),sQuery(id+"F2.wireOp",EDGE,"E7.3.0"),sQuery(id+"F2.wireOp",EDGE,"E7.3.1"),sQuery(id+"F2.wireOp",EDGE,"E7.3.2"),sQuery(id+"F2.wireOp",EDGE,"E7.4.0"),sQuery(id+"F2.wireOp",EDGE,"E7.4.1"),sQuery(id+"F2.wireOp",EDGE,"E7.4.2"),sQuery(id+"F2.wireOp",EDGE,"E7.5.0"),sQuery(id+"F2.wireOp",EDGE,"E7.5.1"),sQuery(id+"F2.wireOp",EDGE,"E7.5.2"),sQuery(id+"F2.wireOp",EDGE,"E7.6.0"),sQuery(id+"F2.wireOp",EDGE,"E7.6.1"),sQuery(id+"F2.wireOp",EDGE,"E7.6.2"),subQ0,sQuery(id+"F2.wireOp",EDGE,"E7.7.1"),sQuery(id+"F2.wireOp",EDGE,"E7.7.2"),sQuery(id+"F2.wireOp",EDGE,"E7.8.0"),sQuery(id+"F2.wireOp",EDGE,"E7.8.1"),sQuery(id+"F2.wireOp",EDGE,"E7.8.2"),sQuery(id+"F2.wireOp",EDGE,"E7.9.0"),sQuery(id+"F2.wireOp",EDGE,"E7.9.1"),sQuery(id+"F2.wireOp",EDGE,"E7.9.2"),sQuery(id+"F2.wireOp",EDGE,"E7.10.0"),sQuery(id+"F2.wireOp",EDGE,"E7.10.1"),sQuery(id+"F2.wireOp",EDGE,"E7.10.2"),sQuery(id+"F2.wireOp",EDGE,"E7.11.0"),sQuery(id+"F2.wireOp",EDGE,"E7.11.1"),sQuery(id+"F2.wireOp",EDGE,"E7.11.2")])],"isStart":true}),makeQuery(id+"F4.opExtrude","CAP_FACE",FACE,{"disambiguationData":[OSD([sQuery(id+"F0.wireOp",EDGE,"E0"),sQuery(id+"F0.wireOp",EDGE,"E1.0"),sQuery(id+"F0.wireOp",EDGE,"E1.1"),sQuery(id+"F0.wireOp",EDGE,"E1.2"),sQuery(id+"F0.wireOp",EDGE,"E1.3"),sQuery(id+"F0.wireOp",EDGE,"E1.4"),sQuery(id+"F0.wireOp",EDGE,"E1.5")])],"isStart":false})]}),makeQuery(id+"F5.opExtrude","SWEPT_FACE",FACE,{"disambiguationData":[OSD([subQ0])]})]});}
            var Q8;
            {var subQ0=sQuery(id+"F2.wireOp",EDGE,"E7.6.0");Q8=makeQuery(id+"F5.boolean.opBoolean","INTERSECT",EDGE,{"derivedFrom":[makeQuery(id+"F4.boolean.opBoolean","MERGE",FACE,{"derivedFrom":[makeQuery(id+"F3.opExtrude","CAP_FACE",FACE,{"disambiguationData":[OSD([sQuery(id+"F2.wireOp",EDGE,"E2.0.0"),sQuery(id+"F2.wireOp",EDGE,"E2.0.1"),sQuery(id+"F2.wireOp",EDGE,"E2.0.2"),sQuery(id+"F2.wireOp",EDGE,"E2.0.3"),sQuery(id+"F2.wireOp",EDGE,"E2.0.4"),sQuery(id+"F2.wireOp",EDGE,"E2.0.5"),sQuery(id+"F2.wireOp",EDGE,"E5.left"),sQuery(id+"F2.wireOp",EDGE,"E4"),sQuery(id+"F2.wireOp",EDGE,"E6"),sQuery(id+"F2.wireOp",EDGE,"E7.1.0"),sQuery(id+"F2.wireOp",EDGE,"E7.1.1"),sQuery(id+"F2.wireOp",EDGE,"E7.1.2"),sQuery(id+"F2.wireOp",EDGE,"E7.2.0"),sQuery(id+"F2.wireOp",EDGE,"E7.2.1"),sQuery(id+"F2.wireOp",EDGE,"E7.2.2"),sQuery(id+"F2.wireOp",EDGE,"E7.3.0"),sQuery(id+"F2.wireOp",EDGE,"E7.3.1"),sQuery(id+"F2.wireOp",EDGE,"E7.3.2"),sQuery(id+"F2.wireOp",EDGE,"E7.4.0"),sQuery(id+"F2.wireOp",EDGE,"E7.4.1"),sQuery(id+"F2.wireOp",EDGE,"E7.4.2"),sQuery(id+"F2.wireOp",EDGE,"E7.5.0"),sQuery(id+"F2.wireOp",EDGE,"E7.5.1"),sQuery(id+"F2.wireOp",EDGE,"E7.5.2"),subQ0,sQuery(id+"F2.wireOp",EDGE,"E7.6.1"),sQuery(id+"F2.wireOp",EDGE,"E7.6.2"),sQuery(id+"F2.wireOp",EDGE,"E7.7.0"),sQuery(id+"F2.wireOp",EDGE,"E7.7.1"),sQuery(id+"F2.wireOp",EDGE,"E7.7.2"),sQuery(id+"F2.wireOp",EDGE,"E7.8.0"),sQuery(id+"F2.wireOp",EDGE,"E7.8.1"),sQuery(id+"F2.wireOp",EDGE,"E7.8.2"),sQuery(id+"F2.wireOp",EDGE,"E7.9.0"),sQuery(id+"F2.wireOp",EDGE,"E7.9.1"),sQuery(id+"F2.wireOp",EDGE,"E7.9.2"),sQuery(id+"F2.wireOp",EDGE,"E7.10.0"),sQuery(id+"F2.wireOp",EDGE,"E7.10.1"),sQuery(id+"F2.wireOp",EDGE,"E7.10.2"),sQuery(id+"F2.wireOp",EDGE,"E7.11.0"),sQuery(id+"F2.wireOp",EDGE,"E7.11.1"),sQuery(id+"F2.wireOp",EDGE,"E7.11.2")])],"isStart":true}),makeQuery(id+"F4.opExtrude","CAP_FACE",FACE,{"disambiguationData":[OSD([sQuery(id+"F0.wireOp",EDGE,"E0"),sQuery(id+"F0.wireOp",EDGE,"E1.0"),sQuery(id+"F0.wireOp",EDGE,"E1.1"),sQuery(id+"F0.wireOp",EDGE,"E1.2"),sQuery(id+"F0.wireOp",EDGE,"E1.3"),sQuery(id+"F0.wireOp",EDGE,"E1.4"),sQuery(id+"F0.wireOp",EDGE,"E1.5")])],"isStart":false})]}),makeQuery(id+"F5.opExtrude","SWEPT_FACE",FACE,{"disambiguationData":[OSD([subQ0])]})]});}
            var Q9;
            {var subQ0=sQuery(id+"F2.wireOp",EDGE,"E7.5.0");Q9=makeQuery(id+"F5.boolean.opBoolean","INTERSECT",EDGE,{"derivedFrom":[makeQuery(id+"F4.boolean.opBoolean","MERGE",FACE,{"derivedFrom":[makeQuery(id+"F3.opExtrude","CAP_FACE",FACE,{"disambiguationData":[OSD([sQuery(id+"F2.wireOp",EDGE,"E2.0.0"),sQuery(id+"F2.wireOp",EDGE,"E2.0.1"),sQuery(id+"F2.wireOp",EDGE,"E2.0.2"),sQuery(id+"F2.wireOp",EDGE,"E2.0.3"),sQuery(id+"F2.wireOp",EDGE,"E2.0.4"),sQuery(id+"F2.wireOp",EDGE,"E2.0.5"),sQuery(id+"F2.wireOp",EDGE,"E5.left"),sQuery(id+"F2.wireOp",EDGE,"E4"),sQuery(id+"F2.wireOp",EDGE,"E6"),sQuery(id+"F2.wireOp",EDGE,"E7.1.0"),sQuery(id+"F2.wireOp",EDGE,"E7.1.1"),sQuery(id+"F2.wireOp",EDGE,"E7.1.2"),sQuery(id+"F2.wireOp",EDGE,"E7.2.0"),sQuery(id+"F2.wireOp",EDGE,"E7.2.1"),sQuery(id+"F2.wireOp",EDGE,"E7.2.2"),sQuery(id+"F2.wireOp",EDGE,"E7.3.0"),sQuery(id+"F2.wireOp",EDGE,"E7.3.1"),sQuery(id+"F2.wireOp",EDGE,"E7.3.2"),sQuery(id+"F2.wireOp",EDGE,"E7.4.0"),sQuery(id+"F2.wireOp",EDGE,"E7.4.1"),sQuery(id+"F2.wireOp",EDGE,"E7.4.2"),subQ0,sQuery(id+"F2.wireOp",EDGE,"E7.5.1"),sQuery(id+"F2.wireOp",EDGE,"E7.5.2"),sQuery(id+"F2.wireOp",EDGE,"E7.6.0"),sQuery(id+"F2.wireOp",EDGE,"E7.6.1"),sQuery(id+"F2.wireOp",EDGE,"E7.6.2"),sQuery(id+"F2.wireOp",EDGE,"E7.7.0"),sQuery(id+"F2.wireOp",EDGE,"E7.7.1"),sQuery(id+"F2.wireOp",EDGE,"E7.7.2"),sQuery(id+"F2.wireOp",EDGE,"E7.8.0"),sQuery(id+"F2.wireOp",EDGE,"E7.8.1"),sQuery(id+"F2.wireOp",EDGE,"E7.8.2"),sQuery(id+"F2.wireOp",EDGE,"E7.9.0"),sQuery(id+"F2.wireOp",EDGE,"E7.9.1"),sQuery(id+"F2.wireOp",EDGE,"E7.9.2"),sQuery(id+"F2.wireOp",EDGE,"E7.10.0"),sQuery(id+"F2.wireOp",EDGE,"E7.10.1"),sQuery(id+"F2.wireOp",EDGE,"E7.10.2"),sQuery(id+"F2.wireOp",EDGE,"E7.11.0"),sQuery(id+"F2.wireOp",EDGE,"E7.11.1"),sQuery(id+"F2.wireOp",EDGE,"E7.11.2")])],"isStart":true}),makeQuery(id+"F4.opExtrude","CAP_FACE",FACE,{"disambiguationData":[OSD([sQuery(id+"F0.wireOp",EDGE,"E0"),sQuery(id+"F0.wireOp",EDGE,"E1.0"),sQuery(id+"F0.wireOp",EDGE,"E1.1"),sQuery(id+"F0.wireOp",EDGE,"E1.2"),sQuery(id+"F0.wireOp",EDGE,"E1.3"),sQuery(id+"F0.wireOp",EDGE,"E1.4"),sQuery(id+"F0.wireOp",EDGE,"E1.5")])],"isStart":false})]}),makeQuery(id+"F5.opExtrude","SWEPT_FACE",FACE,{"disambiguationData":[OSD([subQ0])]})]});}
            var Q10;
            {var subQ0=sQuery(id+"F2.wireOp",EDGE,"E7.4.0");Q10=makeQuery(id+"F5.boolean.opBoolean","INTERSECT",EDGE,{"derivedFrom":[makeQuery(id+"F4.boolean.opBoolean","MERGE",FACE,{"derivedFrom":[makeQuery(id+"F3.opExtrude","CAP_FACE",FACE,{"disambiguationData":[OSD([sQuery(id+"F2.wireOp",EDGE,"E2.0.0"),sQuery(id+"F2.wireOp",EDGE,"E2.0.1"),sQuery(id+"F2.wireOp",EDGE,"E2.0.2"),sQuery(id+"F2.wireOp",EDGE,"E2.0.3"),sQuery(id+"F2.wireOp",EDGE,"E2.0.4"),sQuery(id+"F2.wireOp",EDGE,"E2.0.5"),sQuery(id+"F2.wireOp",EDGE,"E5.left"),sQuery(id+"F2.wireOp",EDGE,"E4"),sQuery(id+"F2.wireOp",EDGE,"E6"),sQuery(id+"F2.wireOp",EDGE,"E7.1.0"),sQuery(id+"F2.wireOp",EDGE,"E7.1.1"),sQuery(id+"F2.wireOp",EDGE,"E7.1.2"),sQuery(id+"F2.wireOp",EDGE,"E7.2.0"),sQuery(id+"F2.wireOp",EDGE,"E7.2.1"),sQuery(id+"F2.wireOp",EDGE,"E7.2.2"),sQuery(id+"F2.wireOp",EDGE,"E7.3.0"),sQuery(id+"F2.wireOp",EDGE,"E7.3.1"),sQuery(id+"F2.wireOp",EDGE,"E7.3.2"),subQ0,sQuery(id+"F2.wireOp",EDGE,"E7.4.1"),sQuery(id+"F2.wireOp",EDGE,"E7.4.2"),sQuery(id+"F2.wireOp",EDGE,"E7.5.0"),sQuery(id+"F2.wireOp",EDGE,"E7.5.1"),sQuery(id+"F2.wireOp",EDGE,"E7.5.2"),sQuery(id+"F2.wireOp",EDGE,"E7.6.0"),sQuery(id+"F2.wireOp",EDGE,"E7.6.1"),sQuery(id+"F2.wireOp",EDGE,"E7.6.2"),sQuery(id+"F2.wireOp",EDGE,"E7.7.0"),sQuery(id+"F2.wireOp",EDGE,"E7.7.1"),sQuery(id+"F2.wireOp",EDGE,"E7.7.2"),sQuery(id+"F2.wireOp",EDGE,"E7.8.0"),sQuery(id+"F2.wireOp",EDGE,"E7.8.1"),sQuery(id+"F2.wireOp",EDGE,"E7.8.2"),sQuery(id+"F2.wireOp",EDGE,"E7.9.0"),sQuery(id+"F2.wireOp",EDGE,"E7.9.1"),sQuery(id+"F2.wireOp",EDGE,"E7.9.2"),sQuery(id+"F2.wireOp",EDGE,"E7.10.0"),sQuery(id+"F2.wireOp",EDGE,"E7.10.1"),sQuery(id+"F2.wireOp",EDGE,"E7.10.2"),sQuery(id+"F2.wireOp",EDGE,"E7.11.0"),sQuery(id+"F2.wireOp",EDGE,"E7.11.1"),sQuery(id+"F2.wireOp",EDGE,"E7.11.2")])],"isStart":true}),makeQuery(id+"F4.opExtrude","CAP_FACE",FACE,{"disambiguationData":[OSD([sQuery(id+"F0.wireOp",EDGE,"E0"),sQuery(id+"F0.wireOp",EDGE,"E1.0"),sQuery(id+"F0.wireOp",EDGE,"E1.1"),sQuery(id+"F0.wireOp",EDGE,"E1.2"),sQuery(id+"F0.wireOp",EDGE,"E1.3"),sQuery(id+"F0.wireOp",EDGE,"E1.4"),sQuery(id+"F0.wireOp",EDGE,"E1.5")])],"isStart":false})]}),makeQuery(id+"F5.opExtrude","SWEPT_FACE",FACE,{"disambiguationData":[OSD([subQ0])]})]});}
            var Q11;
            {var subQ0=sQuery(id+"F2.wireOp",EDGE,"E7.3.0");Q11=makeQuery(id+"F5.boolean.opBoolean","INTERSECT",EDGE,{"derivedFrom":[makeQuery(id+"F4.boolean.opBoolean","MERGE",FACE,{"derivedFrom":[makeQuery(id+"F3.opExtrude","CAP_FACE",FACE,{"disambiguationData":[OSD([sQuery(id+"F2.wireOp",EDGE,"E2.0.0"),sQuery(id+"F2.wireOp",EDGE,"E2.0.1"),sQuery(id+"F2.wireOp",EDGE,"E2.0.2"),sQuery(id+"F2.wireOp",EDGE,"E2.0.3"),sQuery(id+"F2.wireOp",EDGE,"E2.0.4"),sQuery(id+"F2.wireOp",EDGE,"E2.0.5"),sQuery(id+"F2.wireOp",EDGE,"E5.left"),sQuery(id+"F2.wireOp",EDGE,"E4"),sQuery(id+"F2.wireOp",EDGE,"E6"),sQuery(id+"F2.wireOp",EDGE,"E7.1.0"),sQuery(id+"F2.wireOp",EDGE,"E7.1.1"),sQuery(id+"F2.wireOp",EDGE,"E7.1.2"),sQuery(id+"F2.wireOp",EDGE,"E7.2.0"),sQuery(id+"F2.wireOp",EDGE,"E7.2.1"),sQuery(id+"F2.wireOp",EDGE,"E7.2.2"),subQ0,sQuery(id+"F2.wireOp",EDGE,"E7.3.1"),sQuery(id+"F2.wireOp",EDGE,"E7.3.2"),sQuery(id+"F2.wireOp",EDGE,"E7.4.0"),sQuery(id+"F2.wireOp",EDGE,"E7.4.1"),sQuery(id+"F2.wireOp",EDGE,"E7.4.2"),sQuery(id+"F2.wireOp",EDGE,"E7.5.0"),sQuery(id+"F2.wireOp",EDGE,"E7.5.1"),sQuery(id+"F2.wireOp",EDGE,"E7.5.2"),sQuery(id+"F2.wireOp",EDGE,"E7.6.0"),sQuery(id+"F2.wireOp",EDGE,"E7.6.1"),sQuery(id+"F2.wireOp",EDGE,"E7.6.2"),sQuery(id+"F2.wireOp",EDGE,"E7.7.0"),sQuery(id+"F2.wireOp",EDGE,"E7.7.1"),sQuery(id+"F2.wireOp",EDGE,"E7.7.2"),sQuery(id+"F2.wireOp",EDGE,"E7.8.0"),sQuery(id+"F2.wireOp",EDGE,"E7.8.1"),sQuery(id+"F2.wireOp",EDGE,"E7.8.2"),sQuery(id+"F2.wireOp",EDGE,"E7.9.0"),sQuery(id+"F2.wireOp",EDGE,"E7.9.1"),sQuery(id+"F2.wireOp",EDGE,"E7.9.2"),sQuery(id+"F2.wireOp",EDGE,"E7.10.0"),sQuery(id+"F2.wireOp",EDGE,"E7.10.1"),sQuery(id+"F2.wireOp",EDGE,"E7.10.2"),sQuery(id+"F2.wireOp",EDGE,"E7.11.0"),sQuery(id+"F2.wireOp",EDGE,"E7.11.1"),sQuery(id+"F2.wireOp",EDGE,"E7.11.2")])],"isStart":true}),makeQuery(id+"F4.opExtrude","CAP_FACE",FACE,{"disambiguationData":[OSD([sQuery(id+"F0.wireOp",EDGE,"E0"),sQuery(id+"F0.wireOp",EDGE,"E1.0"),sQuery(id+"F0.wireOp",EDGE,"E1.1"),sQuery(id+"F0.wireOp",EDGE,"E1.2"),sQuery(id+"F0.wireOp",EDGE,"E1.3"),sQuery(id+"F0.wireOp",EDGE,"E1.4"),sQuery(id+"F0.wireOp",EDGE,"E1.5")])],"isStart":false})]}),makeQuery(id+"F5.opExtrude","SWEPT_FACE",FACE,{"disambiguationData":[OSD([subQ0])]})]});}
            fillet(context, id + "F10", {"entities" : qUnion([Q0, Q1, Q2, Q3, Q4, Q5, Q6, Q7, Q8, Q9, Q10, Q11]), "radius" : 1.23 * mm, "tangentPropagation" : true, "allowEdgeOverflow" : false});
        }
        {
            var Q0;
            Q0=makeQuery(id+"F1.opExtrude","SWEPT_BODY",BODY,{"disambiguationData":[OSD([sQuery(id+"F0.wireOp",EDGE,"E0"),sQuery(id+"F0.wireOp",EDGE,"E1.0"),sQuery(id+"F0.wireOp",EDGE,"E1.1"),sQuery(id+"F0.wireOp",EDGE,"E1.2"),sQuery(id+"F0.wireOp",EDGE,"E1.3"),sQuery(id+"F0.wireOp",EDGE,"E1.4"),sQuery(id+"F0.wireOp",EDGE,"E1.5")])]});
            deleteBodies(context, id + "F11", {"entities" : qUnion([Q0])});
        }
    });
